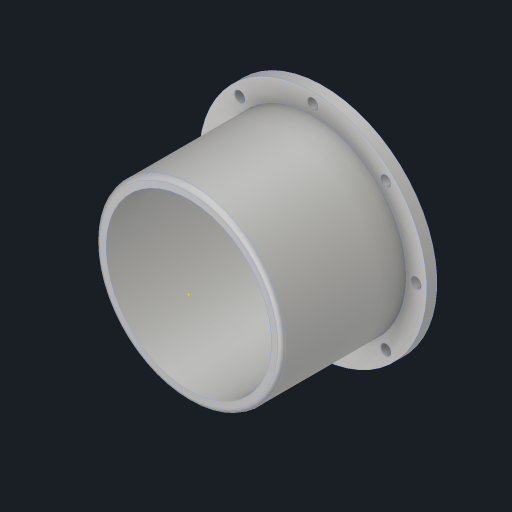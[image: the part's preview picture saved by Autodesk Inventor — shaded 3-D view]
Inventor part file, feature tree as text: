
AUTODESK INVENTOR PART (.ipt)
format: ipt  version: 2023.4 (Build 274418000, 418)  size: 194,048 bytes
history: native  units: mm
features: extrude x4, sketch x3, fillet x1
ambient origin geometry x8: Origin, YZ Plane, XZ Plane, XY Plane, X Axis, Y Axis, Z Axis, Center Point
bodies: Solid1 (feature_tree)
feature tree (8):
  extrude  "Extrusion1"  Depth=5.0mm
  fillet  "Fillet1"  Radius=60.0mm
  extrude  "Extrusion2"  Depth=10.0mm
  extrude  "Extrusion3"  Depth=5.0mm
  extrude  "Extrusion4"  Depth=40.0mm TaperAngle=360.0deg
  sketch  "Sketch5"  dims[d6=5.0mm d7=0.0mm d8=5.0mm d9=40.0mm d11=360.0deg d13=0.0mm d14=0.0mm d18=40.0mm d20=360.0deg d22=0.0mm d23=0.0mm]
  sketch  "Sketch3"  dims[d0=80.0mm d1=5.0mm d2=60.0mm d3=0.0mm]
  sketch  "Sketch4"  dims[d4=2.0mm d5=10.0mm]
